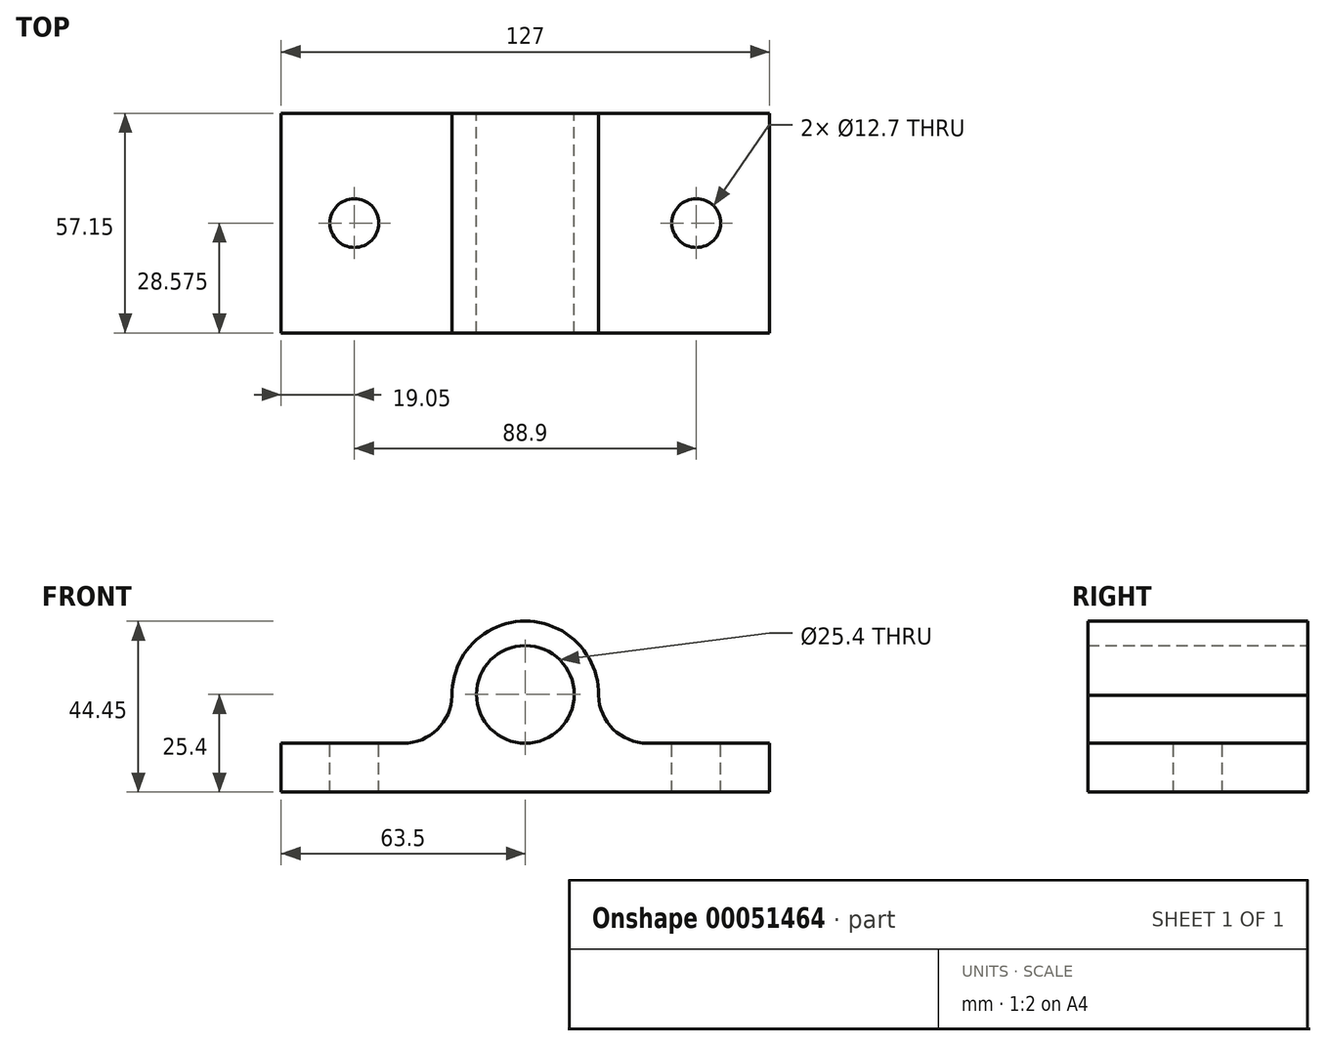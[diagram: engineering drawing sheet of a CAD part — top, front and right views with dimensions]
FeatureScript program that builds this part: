
annotation { "Feature Type Name" : "Feature", "Feature Type Description" : "" }
export const myFeature = defineFeature(function(context is Context, id is Id, definition is map)
    precondition{}
    {
        {
            var Q0;
            Q0=qCreatedBy(makeId("Front.planeOp"),FACE);
            var sketch = newSketch(context, id + "F0", { "sketchPlane" : qUnion([Q0])});
            skLineSegment(sketch, "E0.bottom", {"start": v(0, 0) * mm, "end": v(-127, 0) * mm});
            skLineSegment(sketch, "E0.top", {"start": v(0, 12.7) * mm, "end": v(-127, 12.7) * mm});
            skLineSegment(sketch, "E0.left", {"start": v(0, 0) * mm, "end": v(0, 12.7) * mm});
            skLineSegment(sketch, "E0.right", {"start": v(-127, 0) * mm, "end": v(-127, 12.7) * mm});
            skLineSegment(sketch, "E1.0", {"start": v(0, 25.4) * mm, "end": v(-127, 25.4) * mm, "construction": true});
            skCircle(sketch, "E2", {"center": v(-63.5, 25.4) * mm, "radius": 12.7 * mm});
            skArc(sketch, "E3", {"start": v(-44.45, 25.17) * mm, "mid": v(-63.54, 44.45) * mm, "end": v(-82.55, 25.09) * mm});
            skArc(sketch, "E4", {"start": v(-95.24, 12.7) * mm, "mid": v(-86.15, 16.53) * mm, "end": v(-82.55, 25.71) * mm});
            skArc(sketch, "E5", {"start": v(-44.45, 25.63) * mm, "mid": v(-40.81, 16.5) * mm, "end": v(-31.75, 12.7) * mm});
            skSolve(sketch);
        }
        {
            var Q0;
            Q0 = qSketchRegion(id + "F0", true);
            extrude(context, id + "F1", {"entities" : qUnion([Q0]), "depth" : 57.15 * mm});
        }
        {
            var Q0;
            Q0=qCreatedBy(makeId("Top.planeOp"),FACE);
            var sketch = newSketch(context, id + "F2", { "sketchPlane" : qUnion([Q0])});
            skCircle(sketch, "E6", {"center": v(-19.05, -28.58) * mm, "radius": 6.35 * mm});
            skCircle(sketch, "E7", {"center": v(-107.95, -28.58) * mm, "radius": 6.35 * mm});
            skSolve(sketch);
        }
        {
            var Q0;
            Q0 = qSketchRegion(id + "F2", true);
            extrude(context, id + "F3", {"entities" : qUnion([Q0]), "operationType" : NewBodyOperationType.ADD, "depth" : 25.4 * mm});
        }
        {
            var Q0;
            Q0=makeQuery(id+"F3.opExtrude","CAP_FACE",FACE,{"disambiguationData":[OSD([sQuery(id+"F2.wireOp",EDGE,"E7")])],"isStart":false});
            var Q1;
            Q1=makeQuery(id+"F3.opExtrude","CAP_FACE",FACE,{"disambiguationData":[OSD([sQuery(id+"F2.wireOp",EDGE,"E6")])],"isStart":false});
            extrude(context, id + "F4", {"entities" : qUnion([Q0, Q1]), "operationType" : NewBodyOperationType.REMOVE, "endBound" : BoundingType.THROUGH_ALL, "oppositeDirection" : true, "depth" : 25.4 * mm});
        }
    });
